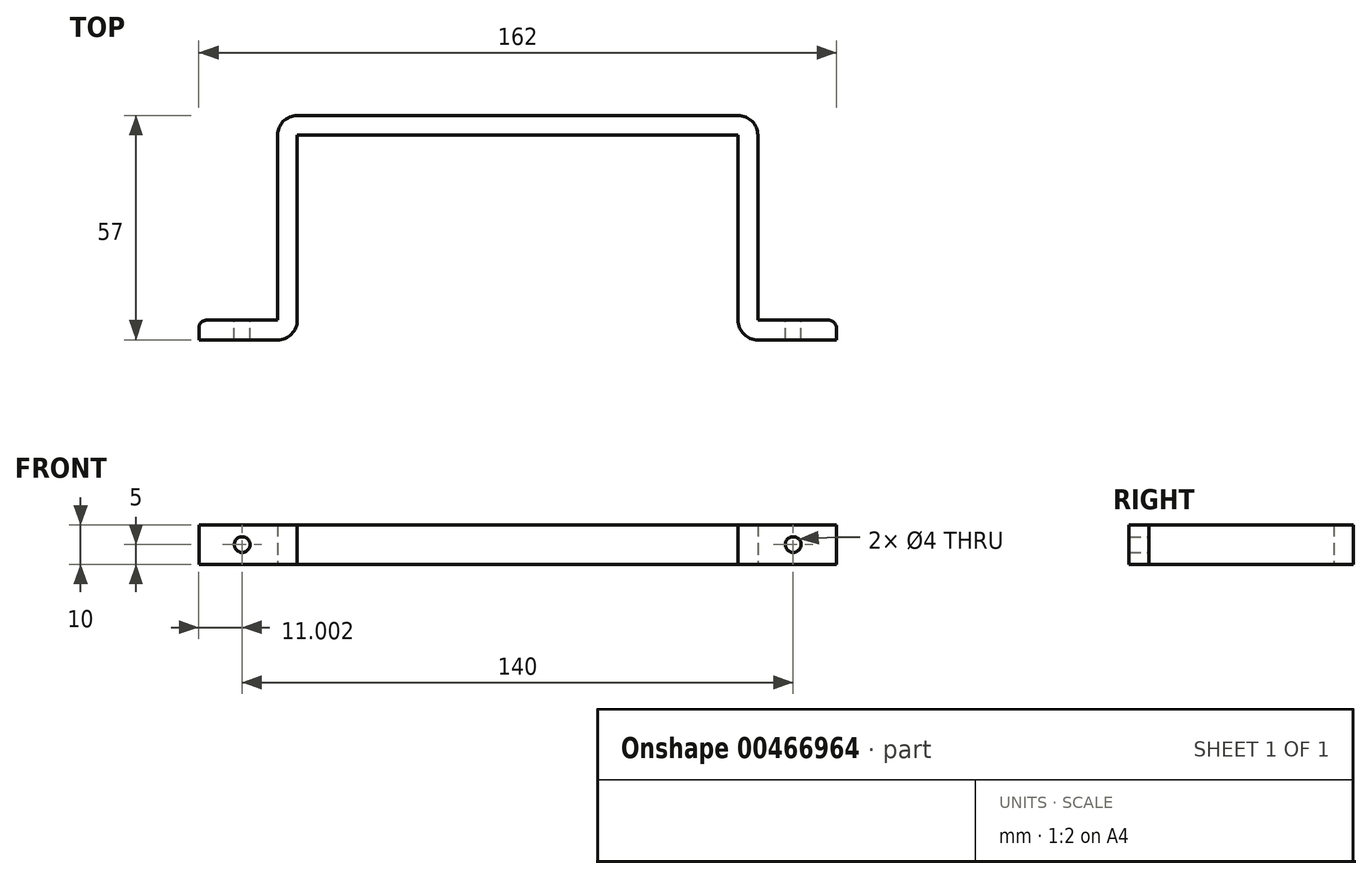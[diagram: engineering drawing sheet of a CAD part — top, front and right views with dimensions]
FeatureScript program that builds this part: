
annotation { "Feature Type Name" : "Feature", "Feature Type Description" : "" }
export const myFeature = defineFeature(function(context is Context, id is Id, definition is map)
    precondition{}
    {
        {
            var Q0;
            Q0=qCreatedBy(makeId("Top.planeOp"),FACE);
            var sketch = newSketch(context, id + "F0", { "sketchPlane" : qUnion([Q0])});
            skLineSegment(sketch, "E0.top", {"start": v(-49.07, 52) * mm, "end": v(62.93, 52) * mm});
            skLineSegment(sketch, "E0.left", {"start": v(-49.07, 5) * mm, "end": v(-49.07, 52) * mm});
            skLineSegment(sketch, "E0.right", {"start": v(62.93, 5) * mm, "end": v(62.93, 52) * mm});
            skLineSegment(sketch, "E1", {"start": v(67.93, 0) * mm, "end": v(87.93, 0) * mm});
            skLineSegment(sketch, "E2", {"start": v(87.93, 0) * mm, "end": v(87.93, 3) * mm});
            skLineSegment(sketch, "E3", {"start": v(85.93, 5) * mm, "end": v(67.93, 5) * mm});
            skLineSegment(sketch, "E4", {"start": v(67.93, 5) * mm, "end": v(67.93, 52) * mm});
            skLineSegment(sketch, "E5", {"start": v(62.93, 57) * mm, "end": v(-49.07, 57) * mm});
            skLineSegment(sketch, "E6", {"start": v(-54.07, 52) * mm, "end": v(-54.07, 5) * mm});
            skLineSegment(sketch, "E7", {"start": v(-54.07, 5) * mm, "end": v(-72.07, 5) * mm});
            skLineSegment(sketch, "E8", {"start": v(-74.07, 3) * mm, "end": v(-74.07, 0) * mm});
            skLineSegment(sketch, "E9", {"start": v(-74.07, 0) * mm, "end": v(-54.07, 0) * mm});
            skPoint(sketch, "E10.visualSharp", {"position": v(-54.07, 57) * mm});
            skArc(sketch, "E10.filletArc", {"start": v(-49.07, 57) * mm, "mid": v(-52.6, 55.54) * mm, "end": v(-54.07, 52) * mm});
            skPoint(sketch, "E11.visualSharp", {"position": v(67.93, 57) * mm});
            skArc(sketch, "E11.filletArc", {"start": v(67.93, 52) * mm, "mid": v(66.47, 55.54) * mm, "end": v(62.93, 57) * mm});
            skPoint(sketch, "E12.visualSharp", {"position": v(62.93, 0) * mm});
            skArc(sketch, "E12.filletArc", {"start": v(62.93, 5) * mm, "mid": v(64.4, 1.46) * mm, "end": v(67.93, 0) * mm});
            skPoint(sketch, "E13.visualSharp", {"position": v(-49.07, 0) * mm});
            skArc(sketch, "E13.filletArc", {"start": v(-54.07, 0) * mm, "mid": v(-50.53, 1.46) * mm, "end": v(-49.07, 5) * mm});
            skPoint(sketch, "E14.visualSharp", {"position": v(-74.07, 5) * mm});
            skArc(sketch, "E14.filletArc", {"start": v(-72.07, 5) * mm, "mid": v(-73.48, 4.41) * mm, "end": v(-74.07, 3) * mm});
            skPoint(sketch, "E15.visualSharp", {"position": v(87.93, 5) * mm});
            skArc(sketch, "E15.filletArc", {"start": v(87.93, 3) * mm, "mid": v(87.35, 4.41) * mm, "end": v(85.93, 5) * mm});
            skSolve(sketch);
        }
        {
            var Q0;
            Q0=makeQuery(id+"F0.imprint","IMPRINT",FACE,{"disambiguationData":[TD([[makeQuery(id+"F0.imprint","IMPRINT",EDGE,{"derivedFrom":sQuery(id+"F0.wireOp",EDGE,"E0.top")}),1.0]])]});
            extrude(context, id + "F1", {"entities" : qUnion([Q0]), "depth" : 10 * mm});
        }
        {
            var Q0;
            Q0=makeQuery(id+"F1.opExtrude","SWEPT_FACE",FACE,{"disambiguationData":[OSD([sQuery(id+"F0.wireOp",EDGE,"E7")])]});
            var sketch = newSketch(context, id + "F2", { "sketchPlane" : qUnion([Q0])});
            skLineSegment(sketch, "E16", {"start": v(63.07, 0) * mm, "end": v(63.07, 10) * mm, "construction": true});
            skLineSegment(sketch, "E17", {"start": v(72.07, 5) * mm, "end": v(54.07, 5) * mm, "construction": true});
            skCircle(sketch, "E18", {"center": v(63.07, 5) * mm, "radius": 2 * mm});
            skSolve(sketch);
        }
        {
            var Q0;
            Q0=makeQuery(id+"F1.opExtrude","SWEPT_FACE",FACE,{"disambiguationData":[OSD([sQuery(id+"F0.wireOp",EDGE,"E3")])]});
            var sketch = newSketch(context, id + "F3", { "sketchPlane" : qUnion([Q0])});
            skLineSegment(sketch, "E19", {"start": v(-67.93, 5) * mm, "end": v(-85.93, 5) * mm, "construction": true});
            skLineSegment(sketch, "E20", {"start": v(-76.93, 0) * mm, "end": v(-76.93, 10) * mm, "construction": true});
            skCircle(sketch, "E21", {"center": v(-76.93, 5) * mm, "radius": 2 * mm});
            skSolve(sketch);
        }
        {
            var Q0;
            Q0=makeQuery(id+"F2.imprint","IMPRINT",FACE,{"disambiguationData":[TD([[makeQuery(id+"F2.imprint","IMPRINT",EDGE,{"derivedFrom":sQuery(id+"F2.wireOp",EDGE,"E18")}),1.0]])]});
            var Q1;
            Q1=makeQuery(id+"F3.imprint","IMPRINT",FACE,{"disambiguationData":[TD([[makeQuery(id+"F3.imprint","IMPRINT",EDGE,{"derivedFrom":sQuery(id+"F3.wireOp",EDGE,"E21")}),1.0]])]});
            extrude(context, id + "F4", {"entities" : qUnion([Q0, Q1]), "operationType" : NewBodyOperationType.REMOVE, "oppositeDirection" : true, "depth" : 25 * mm});
        }
    });
